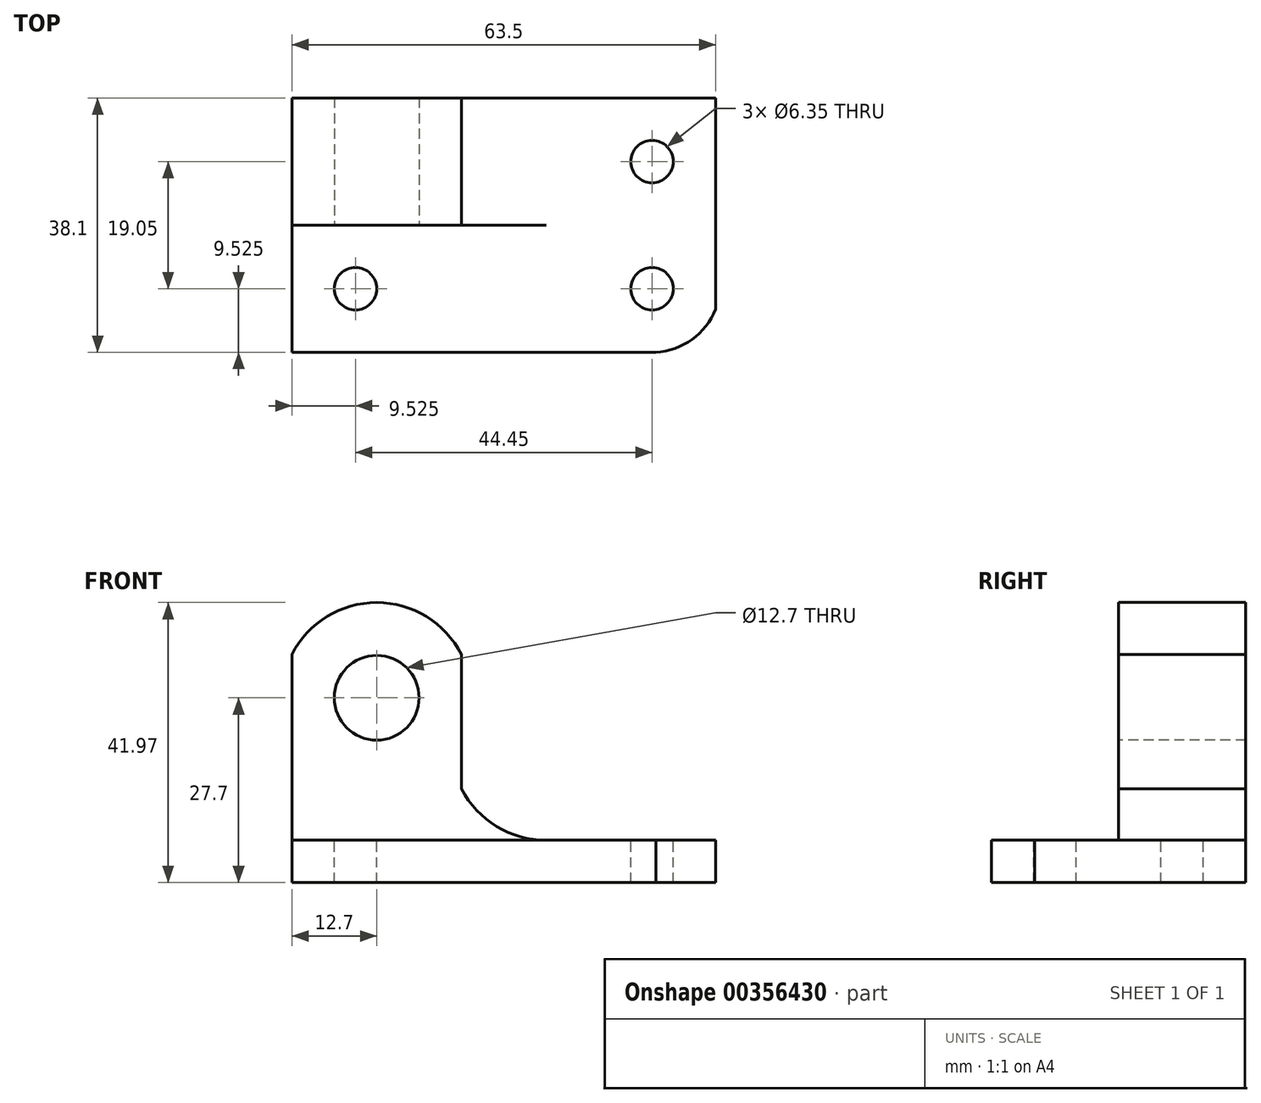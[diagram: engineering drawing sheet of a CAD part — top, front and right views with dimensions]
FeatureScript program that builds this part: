
annotation { "Feature Type Name" : "Feature", "Feature Type Description" : "" }
export const myFeature = defineFeature(function(context is Context, id is Id, definition is map)
    precondition{}
    {
        {
            var Q0;
            Q0=qCreatedBy(makeId("Front.planeOp"),FACE);
            var sketch = newSketch(context, id + "F0", { "sketchPlane" : qUnion([Q0])});
            skLineSegment(sketch, "E0", {"start": v(0, 44.45) * mm, "end": v(0, 0) * mm});
            skLineSegment(sketch, "E1", {"start": v(0, 0) * mm, "end": v(63.5, 0) * mm});
            skLineSegment(sketch, "E2", {"start": v(63.5, 0) * mm, "end": v(63.5, 44.45) * mm});
            skLineSegment(sketch, "E3", {"start": v(63.5, 44.45) * mm, "end": v(0, 44.45) * mm});
            skSolve(sketch);
        }
        {
            var Q0;
            Q0=makeQuery(id+"F0.imprint","IMPRINT",FACE,{"disambiguationData":[TD([[makeQuery(id+"F0.imprint","IMPRINT",EDGE,{"derivedFrom":sQuery(id+"F0.wireOp",EDGE,"E0")}),1.0]])]});
            extrude(context, id + "F1", {"entities" : qUnion([Q0]), "depth" : 38.1 * mm});
        }
        {
            var Q0;
            Q0=makeQuery(id+"F1.opExtrude","CAP_FACE",FACE,{"disambiguationData":[OSD([sQuery(id+"F0.wireOp",EDGE,"E0"),sQuery(id+"F0.wireOp",EDGE,"E1"),sQuery(id+"F0.wireOp",EDGE,"E2"),sQuery(id+"F0.wireOp",EDGE,"E3")])],"isStart":false});
            var sketch = newSketch(context, id + "F2", { "sketchPlane" : qUnion([Q0])});
            skLineSegment(sketch, "E4", {"start": v(38.1, 44.45) * mm, "end": v(38.1, 6.35) * mm});
            skLineSegment(sketch, "E5", {"start": v(38.1, 6.35) * mm, "end": v(63.5, 6.35) * mm});
            skSolve(sketch);
        }
        {
            var Q0;
            Q0 = qSketchRegion(id + "F2", true);
            var Q1;
            {var subQ0=sQuery(id+"F2.wireOp",EDGE,"E4");Q1=makeQuery(id+"F2.imprint","IMPRINT",FACE,{"disambiguationData":[TD([[makeQuery(id+"F2.imprint","IMPRINT",EDGE,{"derivedFrom":subQ0}),1.0]])]});}
            extrude(context, id + "F3", {"entities" : qUnion([Q0, Q1]), "operationType" : NewBodyOperationType.REMOVE, "oppositeDirection" : true, "depth" : 38.1 * mm});
        }
        {
            var Q0;
            Q0=makeQuery(id+"F3.boolean.opBoolean","COPY",FACE,{"derivedFrom":makeQuery(id+"F3.opExtrude","SWEPT_FACE",FACE,{"disambiguationData":[OSD([sQuery(id+"F2.wireOp",EDGE,"E4")])]})});
            var sketch = newSketch(context, id + "F4", { "sketchPlane" : qUnion([Q0])});
            skLineSegment(sketch, "E6", {"start": v(-19.05, 44.45) * mm, "end": v(-19.05, 6.35) * mm});
            skLineSegment(sketch, "E7", {"start": v(-19.05, 6.35) * mm, "end": v(-38.1, 6.35) * mm});
            skSolve(sketch);
        }
        {
            var Q0;
            Q0 = qSketchRegion(id + "F4", true);
            var Q1;
            {var subQ0=sQuery(id+"F4.wireOp",EDGE,"E6");Q1=makeQuery(id+"F4.imprint","IMPRINT",FACE,{"disambiguationData":[TD([[makeQuery(id+"F4.imprint","IMPRINT",EDGE,{"derivedFrom":subQ0}),-1.0]])]});}
            extrude(context, id + "F5", {"entities" : qUnion([Q0, Q1]), "operationType" : NewBodyOperationType.REMOVE, "oppositeDirection" : true, "depth" : 38.1 * mm});
        }
        {
            var Q0;
            Q0=makeQuery(id+"F5.boolean.opBoolean","MERGE",FACE,{"derivedFrom":[makeQuery(id+"F3.boolean.opBoolean","COPY",FACE,{"derivedFrom":makeQuery(id+"F3.opExtrude","SWEPT_FACE",FACE,{"disambiguationData":[OSD([sQuery(id+"F2.wireOp",EDGE,"E5")])]})}),makeQuery(id+"F5.opExtrude","SWEPT_FACE",FACE,{"disambiguationData":[OSD([sQuery(id+"F4.wireOp",EDGE,"E7")])]})]});
            var sketch = newSketch(context, id + "F6", { "sketchPlane" : qUnion([Q0])});
            skCircle(sketch, "E8", {"center": v(53.97, -9.53) * mm, "radius": 3.18 * mm});
            skCircle(sketch, "E9", {"center": v(53.98, -28.58) * mm, "radius": 3.17 * mm});
            skCircle(sketch, "E10", {"center": v(9.53, -28.57) * mm, "radius": 3.18 * mm});
            skSolve(sketch);
        }
        {
            var Q0;
            Q0 = qSketchRegion(id + "F6", true);
            extrude(context, id + "F7", {"entities" : qUnion([Q0]), "operationType" : NewBodyOperationType.REMOVE, "oppositeDirection" : true, "depth" : 25.4 * mm});
        }
        {
            var Q0;
            Q0=makeQuery(id+"F5.boolean.opBoolean","MERGE",FACE,{"derivedFrom":[makeQuery(id+"F3.boolean.opBoolean","COPY",FACE,{"derivedFrom":makeQuery(id+"F3.opExtrude","SWEPT_FACE",FACE,{"disambiguationData":[OSD([sQuery(id+"F2.wireOp",EDGE,"E5")])]})}),makeQuery(id+"F5.opExtrude","SWEPT_FACE",FACE,{"disambiguationData":[OSD([sQuery(id+"F4.wireOp",EDGE,"E7")])]})]});
            var sketch = newSketch(context, id + "F8", { "sketchPlane" : qUnion([Q0])});
            skArc(sketch, "E11", {"start": v(0, -28.57) * mm, "mid": v(1.84, -34.96) * mm, "end": v(7.7, -38.1) * mm});
            skArc(sketch, "E12", {"start": v(54.54, -38.1) * mm, "mid": v(59.96, -36.17) * mm, "end": v(63.5, -31.63) * mm});
            skSolve(sketch);
        }
        {
            var Q0;
            Q0 = qSketchRegion(id + "F8", true);
            var Q1;
            {var subQ0=sQuery(id+"F8.wireOp",EDGE,"E11");var subQ1=sQuery(id+"F4.wireOp",EDGE,"E7");var subQ4=makeQuery(id+"F5.boolean.opBoolean","COPY",EDGE,{"derivedFrom":makeQuery(id+"F5.opExtrude","CAP_EDGE",EDGE,{"disambiguationData":[OSD([subQ1])],"isStart":false})});var subQ5=makeQuery(id+"F8.imprint","INTERSECT",VERTEX,{"disambiguationData":[OD(1.0)],"derivedFrom":[subQ4,subQ0]});Q1=makeQuery(id+"F8.imprint","IMPRINT",FACE,{"disambiguationData":[TD([[makeQuery(id+"F8.imprint","IMPRINT",EDGE,{"disambiguationData":[TD([[subQ5,-1.0]])],"derivedFrom":subQ0}),-1.0]])]});}
            var Q2;
            {var subQ0=sQuery(id+"F8.wireOp",EDGE,"E12");Q2=makeQuery(id+"F8.imprint","IMPRINT",FACE,{"disambiguationData":[TD([[makeQuery(id+"F8.imprint","IMPRINT",EDGE,{"derivedFrom":subQ0}),-1.0]])]});}
            extrude(context, id + "F9", {"entities" : qUnion([Q0, Q1, Q2]), "operationType" : NewBodyOperationType.REMOVE, "oppositeDirection" : true, "depth" : 25.4 * mm});
        }
        {
            var Q0;
            Q0=makeQuery(id+"F5.boolean.opBoolean","COPY",FACE,{"derivedFrom":makeQuery(id+"F5.opExtrude","SWEPT_FACE",FACE,{"disambiguationData":[OSD([sQuery(id+"F4.wireOp",EDGE,"E6")])]})});
            var sketch = newSketch(context, id + "F10", { "sketchPlane" : qUnion([Q0])});
            skLineSegment(sketch, "E13", {"start": v(25.4, 34.2) * mm, "end": v(25.4, 14.04) * mm});
            skArc(sketch, "E14", {"start": v(25.4, 14.04) * mm, "mid": v(30.68, 8.42) * mm, "end": v(38.1, 6.35) * mm});
            skArc(sketch, "E15", {"start": v(25.4, 34.2) * mm, "mid": v(12.7, 41.97) * mm, "end": v(0, 34.2) * mm});
            skSolve(sketch);
        }
        {
            var Q0;
            Q0 = qSketchRegion(id + "F10", true);
            var Q1;
            Q1=makeQuery(id+"F10.imprint","IMPRINT",FACE,{"disambiguationData":[TD([[makeQuery(id+"F10.imprint","IMPRINT",EDGE,{"derivedFrom":sQuery(id+"F10.wireOp",EDGE,"E13")}),1.0]])]});
            extrude(context, id + "F11", {"entities" : qUnion([Q0, Q1]), "operationType" : NewBodyOperationType.REMOVE, "oppositeDirection" : true, "depth" : 25.4 * mm});
        }
        {
            var Q0;
            Q0=makeQuery(id+"F5.boolean.opBoolean","COPY",FACE,{"derivedFrom":makeQuery(id+"F5.opExtrude","SWEPT_FACE",FACE,{"disambiguationData":[OSD([sQuery(id+"F4.wireOp",EDGE,"E6")])]})});
            var sketch = newSketch(context, id + "F12", { "sketchPlane" : qUnion([Q0])});
            skCircle(sketch, "E16", {"center": v(12.7, 27.7) * mm, "radius": 6.35 * mm});
            skSolve(sketch);
        }
        {
            var Q0;
            Q0=makeQuery(id+"F12.imprint","IMPRINT",FACE,{"disambiguationData":[TD([[makeQuery(id+"F12.imprint","IMPRINT",EDGE,{"derivedFrom":sQuery(id+"F12.wireOp",EDGE,"E16")}),1.0]])]});
            extrude(context, id + "F13", {"entities" : qUnion([Q0]), "operationType" : NewBodyOperationType.REMOVE, "oppositeDirection" : true, "depth" : 25.4 * mm});
        }
    });
